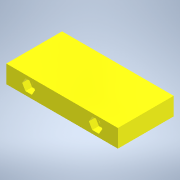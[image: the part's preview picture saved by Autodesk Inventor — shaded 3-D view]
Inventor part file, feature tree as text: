
AUTODESK INVENTOR PART (.ipt)
format: ipt  version: 2020 (Build 240168000, 168)  size: 147,456 bytes
history: native  units: mm
features: sketch x5, extrude x4, hole x1
ambient origin geometry x8: Origin, YZ Plane, XZ Plane, XY Plane, X Axis, Y Axis, Z Axis, Center Point
bodies: Solido1 (feature_tree)
feature tree (10):
  extrude  "Estrusione1"  Depth=50.0mm
  extrude  "Estrusione2"  Depth=16.0mm TaperAngle=0.0deg
  extrude  "Estrusione3"  Depth=19.0mm
  hole  "Foro1"  [1 undecoded]
  extrude  "Estrusione4"  Depth=12.0mm
  sketch  "Schizzo1"
  sketch  "Schizzo2"
  sketch  "Schizzo3"
  sketch  "Schizzo4"
  sketch  "Schizzo5"
note: 1 required parameter value undecoded (feature->parameter linkage not recoverable at this tier; creation-order binding heuristic only, values carry confidence <= 0.55)
